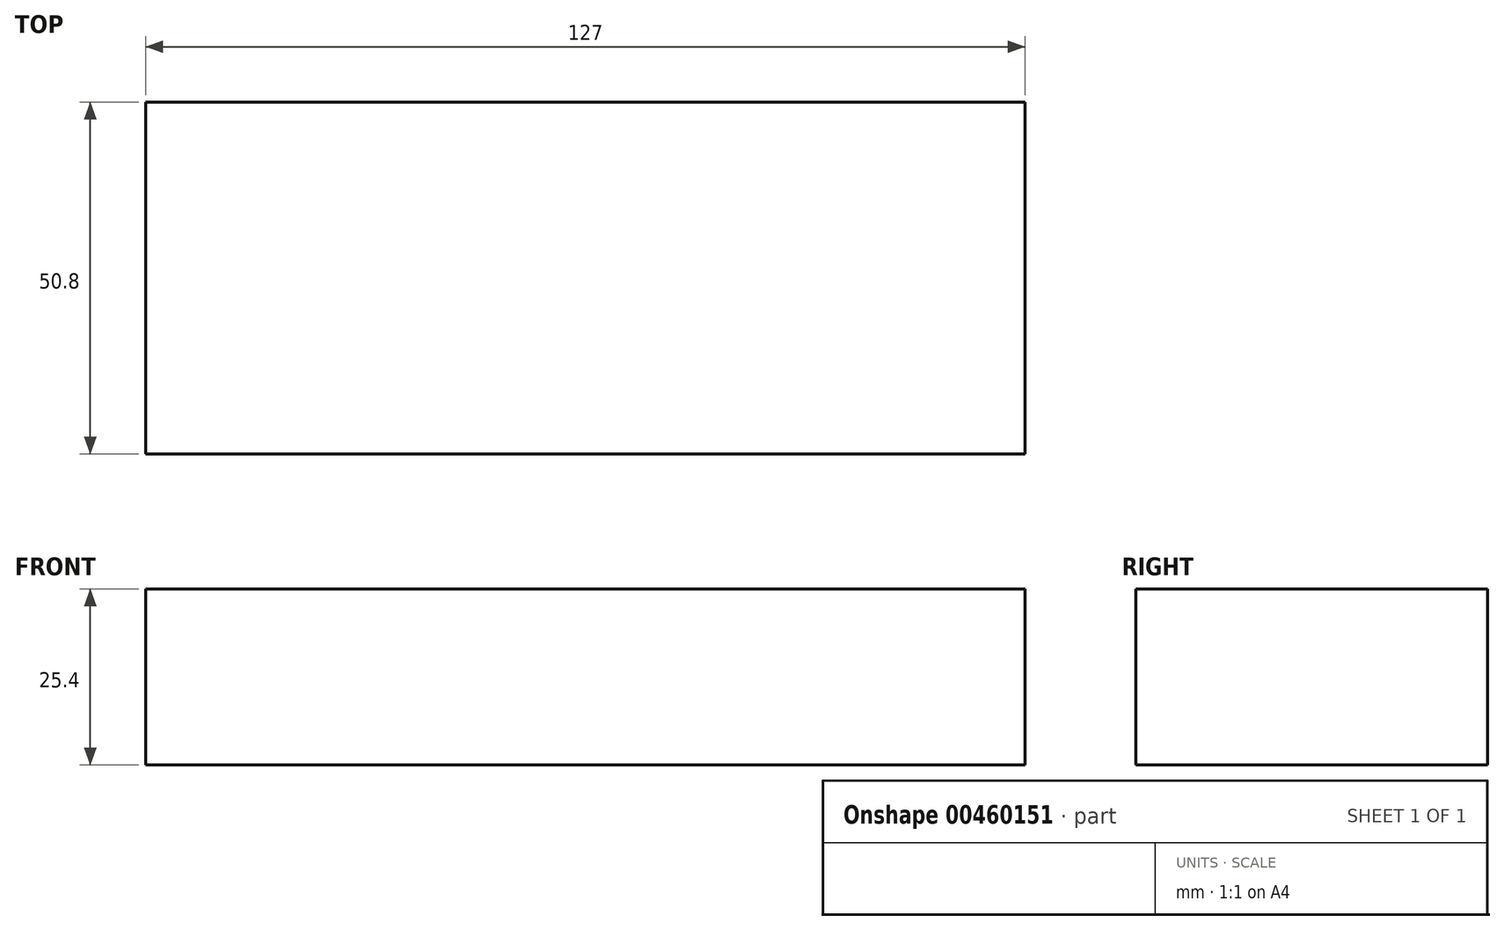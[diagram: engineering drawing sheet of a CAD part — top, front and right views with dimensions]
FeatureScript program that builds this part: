
annotation { "Feature Type Name" : "Feature", "Feature Type Description" : "" }
export const myFeature = defineFeature(function(context is Context, id is Id, definition is map)
    precondition{}
    {
        {
            var Q0;
            Q0=qCreatedBy(makeId("Top.planeOp"),FACE);
            var sketch = newSketch(context, id + "F0", { "sketchPlane" : qUnion([Q0])});
            skLineSegment(sketch, "E0.bottom", {"start": v(63.5, -25.4) * mm, "end": v(-63.5, -25.4) * mm});
            skLineSegment(sketch, "E0.top", {"start": v(63.5, 25.4) * mm, "end": v(-63.5, 25.4) * mm});
            skLineSegment(sketch, "E0.left", {"start": v(63.5, -25.4) * mm, "end": v(63.5, 25.4) * mm});
            skLineSegment(sketch, "E0.right", {"start": v(-63.5, -25.4) * mm, "end": v(-63.5, 25.4) * mm});
            skPoint(sketch, "E0.middle", {"position": v(0, 0) * mm});
            skSolve(sketch);
        }
        {
            var Q0;
            Q0 = qSketchRegion(id + "F0", true);
            extrude(context, id + "F1", {"entities" : qUnion([Q0]), "depth" : 25.4 * mm});
        }
    });
